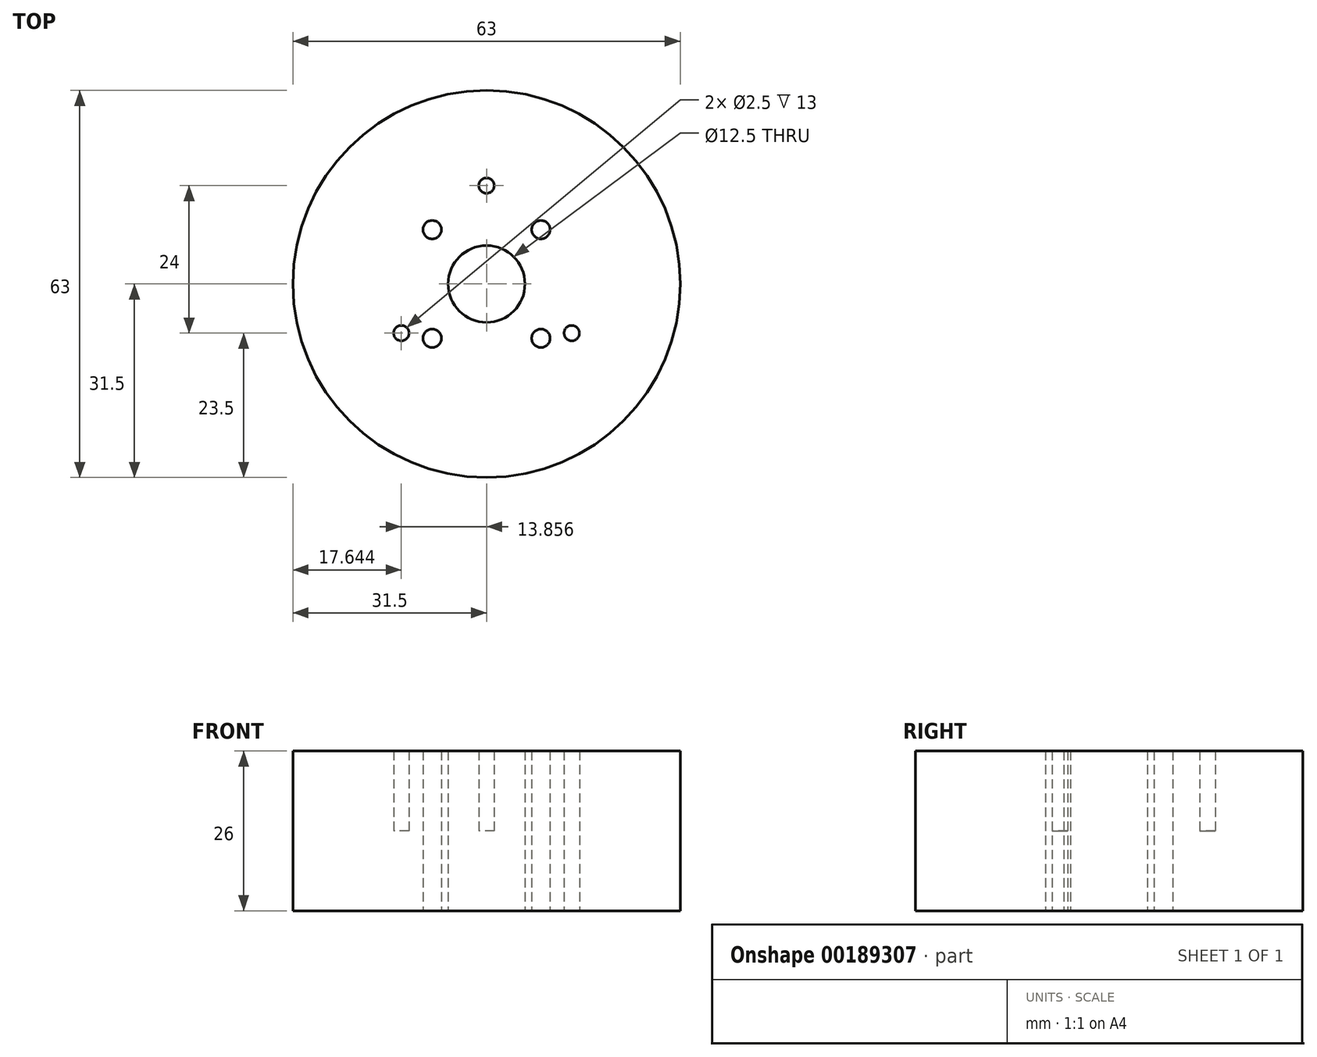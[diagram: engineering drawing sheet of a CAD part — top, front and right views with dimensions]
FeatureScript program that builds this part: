
annotation { "Feature Type Name" : "Feature", "Feature Type Description" : "" }
export const myFeature = defineFeature(function(context is Context, id is Id, definition is map)
    precondition{}
    {
        {
            var Q0;
            Q0=qCreatedBy(makeId("Top.planeOp"),FACE);
            var sketch = newSketch(context, id + "F0", { "sketchPlane" : qUnion([Q0])});
            skCircle(sketch, "E0", {"center": v(0, 0) * mm, "radius": 31.5 * mm});
            skCircle(sketch, "E1", {"center": v(0, 0) * mm, "radius": 16 * mm});
            skCircle(sketch, "E2", {"center": v(-8.84, 8.84) * mm, "radius": 1.5 * mm});
            skCircle(sketch, "E3", {"center": v(0, 16) * mm, "radius": 1.25 * mm});
            skCircle(sketch, "E4", {"center": v(-13.86, -8) * mm, "radius": 1.25 * mm});
            skCircle(sketch, "E5", {"center": v(0, 0) * mm, "radius": 6.25 * mm});
            skCircle(sketch, "E6.MirrorC", {"center": v(8.84, 8.84) * mm, "radius": 1.5 * mm});
            skCircle(sketch, "E7.MirrorC", {"center": v(8.84, -8.84) * mm, "radius": 1.5 * mm});
            skCircle(sketch, "E8.MirrorC", {"center": v(-8.84, -8.84) * mm, "radius": 1.5 * mm});
            skCircle(sketch, "E9.MirrorC", {"center": v(13.86, -8) * mm, "radius": 1.25 * mm});
            skSolve(sketch);
        }
        {
            var Q0;
            Q0=makeQuery(id+"F0.imprint","IMPRINT",FACE,{"disambiguationData":[TD([[makeQuery(id+"F0.imprint","IMPRINT",EDGE,{"derivedFrom":sQuery(id+"F0.wireOp",EDGE,"E0")}),1.0]])]});
            var Q1;
            Q1=makeQuery(id+"F0.imprint","IMPRINT",FACE,{"disambiguationData":[TD([[makeQuery(id+"F0.imprint","IMPRINT",EDGE,{"derivedFrom":sQuery(id+"F0.wireOp",EDGE,"E2")}),-1.0]])]});
            extrude(context, id + "F1", {"entities" : qUnion([Q0, Q1]), "depth" : 13 * mm});
        }
        {
            var Q0;
            Q0=makeQuery(id+"F0.imprint","IMPRINT",FACE,{"disambiguationData":[TD([[makeQuery(id+"F0.imprint","IMPRINT",EDGE,{"derivedFrom":sQuery(id+"F0.wireOp",EDGE,"E0")}),1.0]])]});
            var Q1;
            Q1=makeQuery(id+"F0.imprint","IMPRINT",FACE,{"disambiguationData":[TD([[makeQuery(id+"F0.imprint","IMPRINT",EDGE,{"derivedFrom":sQuery(id+"F0.wireOp",EDGE,"E2")}),-1.0]])]});
            var Q2;
            {var subQ0=sQuery(id+"F0.wireOp",EDGE,"E4");var subQ1=sQuery(id+"F0.wireOp",EDGE,"E1");var subQ2=makeQuery(id+"F0.imprint","INTERSECT",VERTEX,{"disambiguationData":[OD(0.0)],"derivedFrom":[subQ1,subQ0]});Q2=makeQuery(id+"F0.imprint","IMPRINT",FACE,{"disambiguationData":[TD([[makeQuery(id+"F0.imprint","IMPRINT",EDGE,{"disambiguationData":[TD([[subQ2,-1.0]])],"derivedFrom":subQ1}),1.0]])]});}
            var Q3;
            {var subQ0=sQuery(id+"F0.wireOp",EDGE,"E4");var subQ1=sQuery(id+"F0.wireOp",EDGE,"E1");var subQ2=makeQuery(id+"F0.imprint","INTERSECT",VERTEX,{"disambiguationData":[OD(0.0)],"derivedFrom":[subQ1,subQ0]});Q3=makeQuery(id+"F0.imprint","IMPRINT",FACE,{"disambiguationData":[TD([[makeQuery(id+"F0.imprint","IMPRINT",EDGE,{"disambiguationData":[TD([[subQ2,-1.0]])],"derivedFrom":subQ1}),-1.0]])]});}
            var Q4;
            {var subQ0=sQuery(id+"F0.wireOp",EDGE,"dda97bd3-6e03-4bf1-9ffe-c466719c1e3a.MirrorC");var subQ1=sQuery(id+"F0.wireOp",EDGE,"E1");var subQ2=makeQuery(id+"F0.imprint","INTERSECT",VERTEX,{"disambiguationData":[OD(0.0)],"derivedFrom":[subQ1,subQ0]});Q4=makeQuery(id+"F0.imprint","IMPRINT",FACE,{"disambiguationData":[TD([[makeQuery(id+"F0.imprint","IMPRINT",EDGE,{"disambiguationData":[TD([[subQ2,-1.0]])],"derivedFrom":subQ1}),1.0]])]});}
            var Q5;
            {var subQ0=sQuery(id+"F0.wireOp",EDGE,"dda97bd3-6e03-4bf1-9ffe-c466719c1e3a.MirrorC");var subQ1=sQuery(id+"F0.wireOp",EDGE,"E1");var subQ2=makeQuery(id+"F0.imprint","INTERSECT",VERTEX,{"disambiguationData":[OD(0.0)],"derivedFrom":[subQ1,subQ0]});Q5=makeQuery(id+"F0.imprint","IMPRINT",FACE,{"disambiguationData":[TD([[makeQuery(id+"F0.imprint","IMPRINT",EDGE,{"disambiguationData":[TD([[subQ2,-1.0]])],"derivedFrom":subQ1}),-1.0]])]});}
            var Q6;
            {var subQ0=sQuery(id+"F0.wireOp",EDGE,"E3");var subQ1=sQuery(id+"F0.wireOp",EDGE,"E1");var subQ2=makeQuery(id+"F0.imprint","INTERSECT",VERTEX,{"disambiguationData":[OD(0.0)],"derivedFrom":[subQ1,subQ0]});Q6=makeQuery(id+"F0.imprint","IMPRINT",FACE,{"disambiguationData":[TD([[makeQuery(id+"F0.imprint","IMPRINT",EDGE,{"disambiguationData":[TD([[subQ2,1.0]])],"derivedFrom":subQ1}),-1.0]])]});}
            var Q7;
            {var subQ0=sQuery(id+"F0.wireOp",EDGE,"E3");var subQ1=sQuery(id+"F0.wireOp",EDGE,"E1");var subQ2=makeQuery(id+"F0.imprint","INTERSECT",VERTEX,{"disambiguationData":[OD(0.0)],"derivedFrom":[subQ1,subQ0]});Q7=makeQuery(id+"F0.imprint","IMPRINT",FACE,{"disambiguationData":[TD([[makeQuery(id+"F0.imprint","IMPRINT",EDGE,{"disambiguationData":[TD([[subQ2,1.0]])],"derivedFrom":subQ1}),1.0]])]});}
            extrude(context, id + "F2", {"entities" : qUnion([Q0, Q1, Q2, Q3, Q4, Q5, Q6, Q7]), "operationType" : NewBodyOperationType.ADD, "oppositeDirection" : true, "depth" : 13 * mm});
        }
    });
